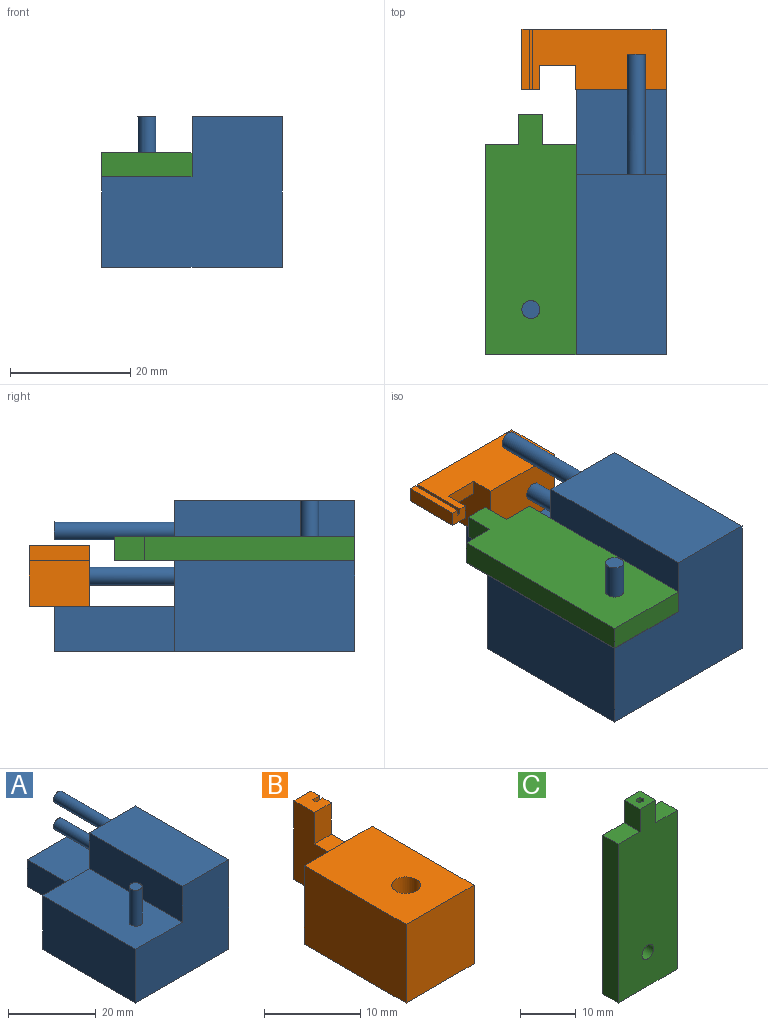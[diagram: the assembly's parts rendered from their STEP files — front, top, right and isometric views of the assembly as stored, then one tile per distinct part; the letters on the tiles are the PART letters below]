
ASSEMBLY  parts=3 mates=2
PART A: 17 faces, bbox 30x50x25 mm
  f0: plane 50x25mm, normal (1,0,0), area 900mm2, adj f1,f4,f5,f8,f10,f12
  f1: plane 15x7.5mm, normal (0,1,0), area 112.5mm2, adj f0,f5,f9,f10
  f2: plane 30x15mm, normal (0,0,1), area 442.9mm2, adj f3,f4,f6,f8,f11
  f3: plane 30x15mm, normal (-1,0,0), area 450mm2, adj f2,f4,f5,f8
  f4: plane 30x25mm, normal (0,-1,0), area 600mm2, adj f0,f2,f3,f5,f11,f12
  f5: plane 50x30mm, normal (0,0,-1), area 1200mm2, adj f0,f1,f3,f4,f8,f9
  f6: cylinder r=1.5mm len=10mm, axis (0,0,-1), area 94.2mm2, adj f2,f7
  f7: plane 3x3mm, normal (0,0,1), area 7.1mm2, adj f6
  f8: plane 30x25mm, normal (0,1,0), area 473.4mm2, adj f0,f2,f3,f5,f9,f10,f11,f12
  f9: plane 20x7.5mm, normal (-1,0,0), area 150mm2, adj f1,f5,f8,f10
  f10: plane 20x15mm, normal (0,0,1), area 300mm2, adj f0,f1,f8,f9
  f11: plane 30x10mm, normal (-1,0,0), area 300mm2, adj f2,f4,f8,f12
  f12: plane 30x15mm, normal (0,0,1), area 450mm2, adj f0,f4,f8,f11
  f13: cylinder r=1.5mm len=20mm, axis (0,-1,0), area 188.5mm2, adj f8,f14
  f14: plane 3x3mm, normal (0,1,0), area 7.1mm2, adj f13
  f15: cylinder r=1.5mm len=20mm, axis (0,-1,0), area 188.5mm2, adj f8,f16
  f16: plane 3x3mm, normal (0,1,0), area 7.1mm2, adj f15
PART B: 16 faces, bbox 10x24x10 mm
  f0: plane 10x9mm, normal (-1,0,0), area 66mm2, adj f1,f9,f10,f13,f14,f15
  f1: plane 3x2.5mm, normal (0,0,1), area 7mm2, adj f0,f4,f5,f6,f7,f8,f9,f15
  f2: plane 15x10mm, normal (-1,0,0), area 150mm2, adj f3,f10,f12,f13
  f3: plane 10x10mm, normal (0,-1,0), area 100mm2, adj f2,f4,f12,f13
  f4: plane 22.25x10mm, normal (1,0,0), area 198.5mm2, adj f1,f3,f5,f10,f12,f13,f14,f15
  f5: plane 10x1mm, normal (0,1,0), area 10mm2, adj f1,f4,f6,f13
  f6: plane 10x0.5mm, normal (1,0,0), area 5mm2, adj f1,f5,f7,f13
  f7: plane 10x1mm, normal (0,-1,0), area 10mm2, adj f1,f6,f8,f13
  f8: plane 10x1.25mm, normal (1,0,0), area 12.5mm2, adj f1,f7,f9,f13
  f9: plane 10x2.5mm, normal (0,1,0), area 25mm2, adj f0,f1,f8,f13
  f10: plane 10x10mm, normal (0,1,0), area 85mm2, adj f0,f2,f4,f12,f13,f14
  f11: cylinder r=1.5mm len=10mm, axis (0,0,-1), area 94.2mm2, adj f12,f13
  f12: plane 15x10mm, normal (0,0,1), area 142.9mm2, adj f2,f3,f4,f10,f11
  f13: plane 24x10mm, normal (0,0,-1), area 164.9mm2, adj f0,f2,f3,f4,f5,f6,f7,f8
  f14: plane 6x2.5mm, normal (0,0,1), area 15mm2, adj f0,f4,f10,f15
  f15: plane 4x2.5mm, normal (0,-1,0), area 10mm2, adj f0,f1,f4,f14
PART C: 13 faces, bbox 15x4x40 mm
  f0: plane 35x4mm, normal (-1,0,0), area 140mm2, adj f1,f7,f9,f10
  f1: plane 15x4mm, normal (0,0,-1), area 60mm2, adj f0,f2,f9,f10
  f2: plane 35x4mm, normal (1,0,0), area 140mm2, adj f1,f3,f9,f10
  f3: plane 5.5x4mm, normal (0,0,1), area 22mm2, adj f2,f4,f9,f10
  f4: plane 5x4mm, normal (1,0,0), area 20mm2, adj f3,f5,f9,f10
  f5: plane 4x4mm, normal (0,0,1), area 14.7mm2, adj f4,f6,f9,f10,f11
  f6: plane 5x4mm, normal (-1,0,0), area 20mm2, adj f5,f7,f9,f10
  f7: plane 5.5x4mm, normal (0,0,1), area 22mm2, adj f0,f6,f9,f10
  f8: cylinder r=1.5mm len=4mm, axis (0,1,0), area 37.7mm2, adj f9,f10
  f9: plane 40x15mm, normal (0,-1,0), area 537.9mm2, adj f0,f1,f2,f3,f4,f5,f6,f7
  f10: plane 40x15mm, normal (0,1,0), area 537.9mm2, adj f0,f1,f2,f3,f4,f5,f6,f7
  f11: cylinder r=0.65mm len=3mm, axis (0,0,1), area 12.3mm2, adj f5,f12
  f12: plane 1.3x1.3mm, normal (0,0,1), area 1.3mm2, adj f11
PLACE A t=(-3.02,-1.67,-13.17)mm
PLACE B rot(axis=(0.58,-0.58,0.58),120deg) t=(-0.02,27.53,-0.67)mm
PLACE C rot(axis=(-1,0,0),90deg) t=(-10.52,-6.67,1.89)mm
MATE slider B.f11 <-> A.f13  axis (0,1,0) through (6.98,27.53,-0.67)mm
MATE slider C.f8 <-> A.f6  axis (0,0,1) through (-10.52,-19.17,5.89)mm
